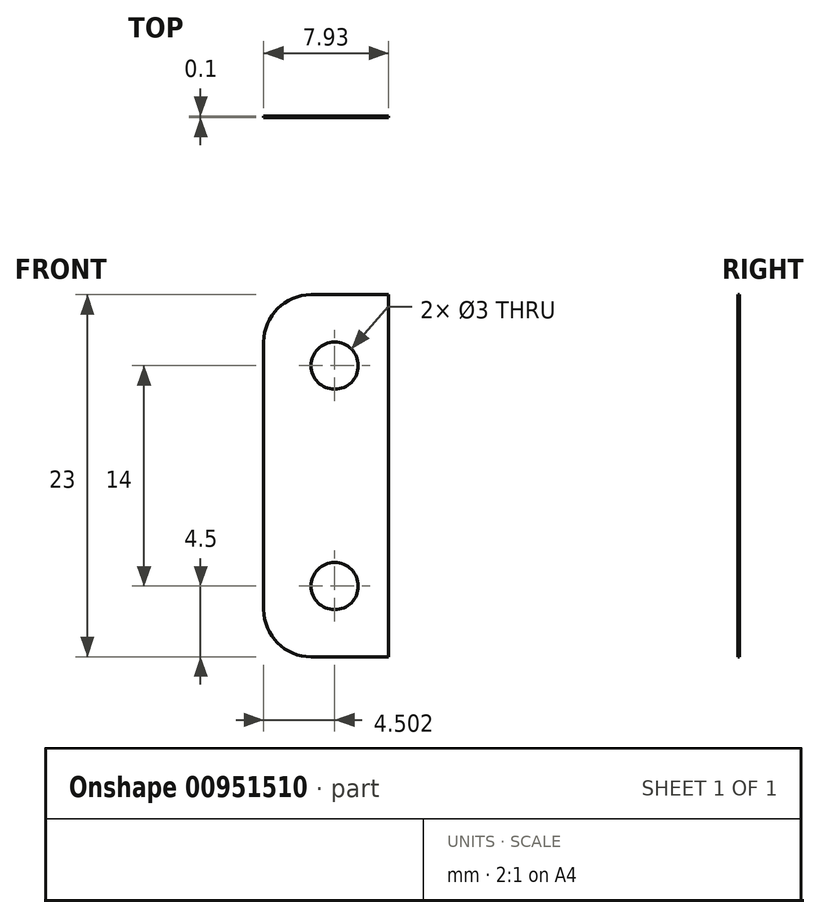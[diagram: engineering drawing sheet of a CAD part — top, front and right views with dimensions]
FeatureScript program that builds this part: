
annotation { "Feature Type Name" : "Feature", "Feature Type Description" : "" }
export const myFeature = defineFeature(function(context is Context, id is Id, definition is map)
    precondition{}
    {
        {
            var Q0;
            Q0=qCreatedBy(makeId("Front.planeOp"),FACE);
            var sketch = newSketch(context, id + "F0", { "sketchPlane" : qUnion([Q0])});
            skLineSegment(sketch, "E0.bottom", {"start": v(-8.43, -11.5) * mm, "end": v(8.43, -11.5) * mm});
            skLineSegment(sketch, "E0.top", {"start": v(-8.43, 11.5) * mm, "end": v(8.43, 11.5) * mm});
            skLineSegment(sketch, "E0.left", {"start": v(-11.43, -8.5) * mm, "end": v(-11.43, 8.5) * mm});
            skLineSegment(sketch, "E0.right", {"start": v(11.43, -8.5) * mm, "end": v(11.43, 8.5) * mm});
            skCircle(sketch, "E1", {"center": v(0, 6) * mm, "radius": 2.5 * mm});
            skCircle(sketch, "E2", {"center": v(0, -6) * mm, "radius": 2.5 * mm});
            skCircle(sketch, "E3", {"center": v(6.93, 7) * mm, "radius": 1.5 * mm});
            skCircle(sketch, "E4", {"center": v(-6.93, 7) * mm, "radius": 1.5 * mm});
            skCircle(sketch, "E5", {"center": v(-6.93, -7) * mm, "radius": 1.5 * mm});
            skCircle(sketch, "E6", {"center": v(6.93, -7) * mm, "radius": 1.5 * mm});
            skPoint(sketch, "E7.visualSharp", {"position": v(11.43, 11.5) * mm});
            skArc(sketch, "E7.filletArc", {"start": v(11.43, 8.5) * mm, "mid": v(10.55, 10.62) * mm, "end": v(8.43, 11.5) * mm});
            skPoint(sketch, "E8.visualSharp", {"position": v(-11.43, 11.5) * mm});
            skArc(sketch, "E8.filletArc", {"start": v(-8.43, 11.5) * mm, "mid": v(-10.55, 10.62) * mm, "end": v(-11.43, 8.5) * mm});
            skPoint(sketch, "E9.visualSharp", {"position": v(-11.43, -11.5) * mm});
            skArc(sketch, "E9.filletArc", {"start": v(-11.43, -8.5) * mm, "mid": v(-10.55, -10.62) * mm, "end": v(-8.43, -11.5) * mm});
            skPoint(sketch, "E10.visualSharp", {"position": v(11.43, -11.5) * mm});
            skArc(sketch, "E10.filletArc", {"start": v(8.43, -11.5) * mm, "mid": v(10.55, -10.62) * mm, "end": v(11.43, -8.5) * mm});
            skLineSegment(sketch, "E11", {"start": v(3.5, 11.5) * mm, "end": v(3.5, -11.5) * mm});
            skLineSegment(sketch, "E12", {"start": v(-3.5, 11.5) * mm, "end": v(-3.5, -11.5) * mm});
            skSolve(sketch);
        }
        {
            var Q0;
            Q0=makeQuery(id+"F0.imprint","IMPRINT",FACE,{"disambiguationData":[TD([[makeQuery(id+"F0.imprint","IMPRINT",EDGE,{"derivedFrom":sQuery(id+"F0.wireOp",EDGE,"E0.left")}),-1.0]])]});
            extrude(context, id + "F1", {"entities" : qUnion([Q0]), "depth" : 0.1 * mm, "offsetDistance" : 25 * mm});
        }
    });
